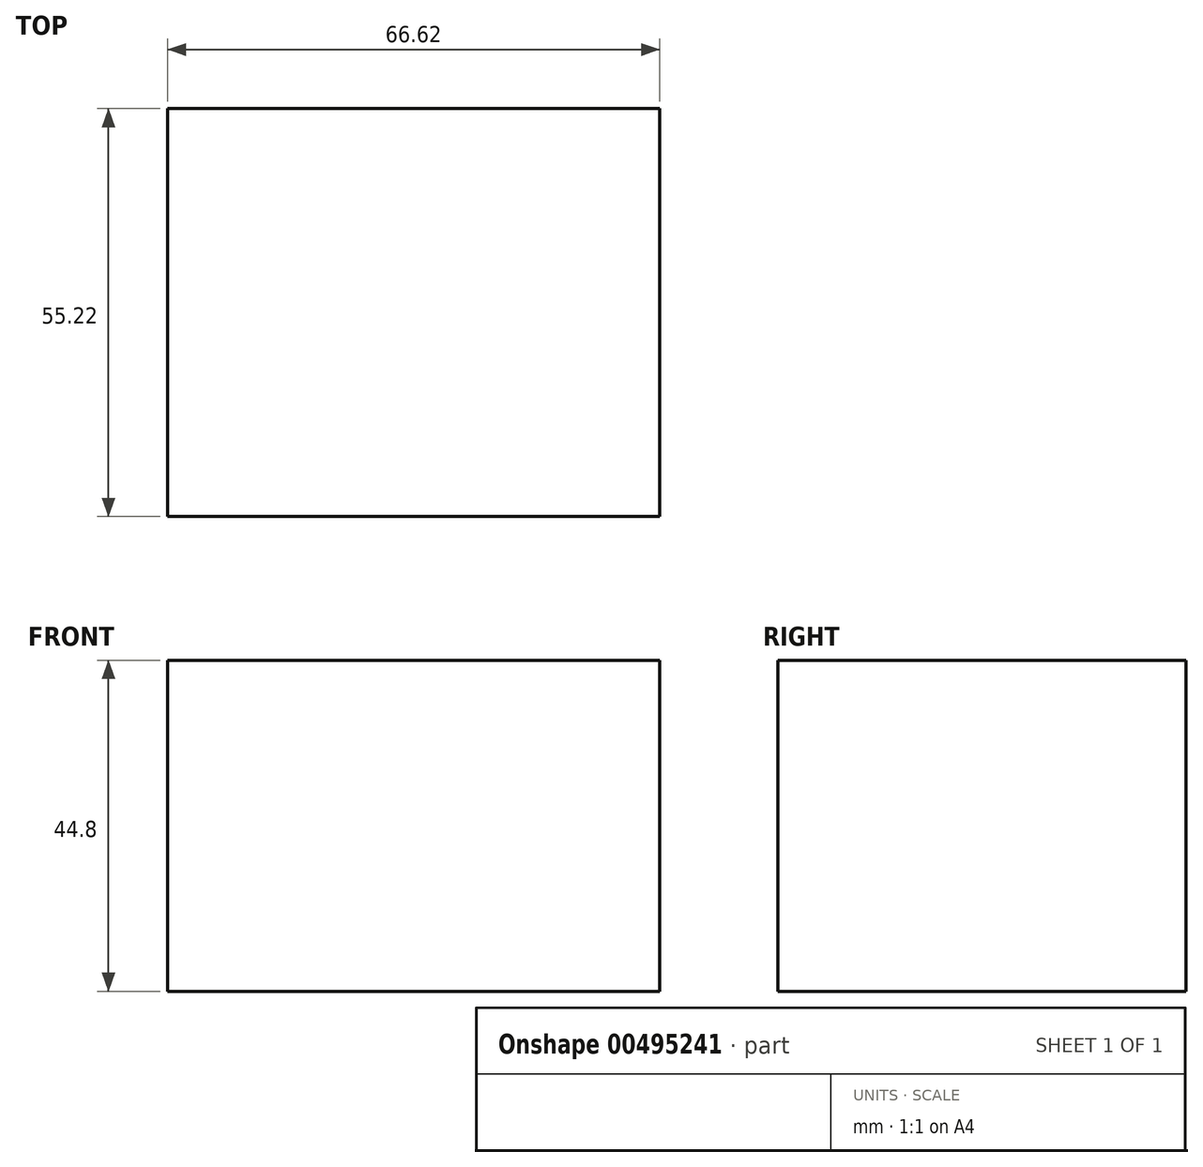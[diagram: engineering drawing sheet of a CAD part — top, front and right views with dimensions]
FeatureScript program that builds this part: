
annotation { "Feature Type Name" : "Feature", "Feature Type Description" : "" }
export const myFeature = defineFeature(function(context is Context, id is Id, definition is map)
    precondition{}
    {
        {
            var Q0;
            Q0=qCreatedBy(makeId("Top.planeOp"),FACE);
            var sketch = newSketch(context, id + "F0", { "sketchPlane" : qUnion([Q0])});
            skLineSegment(sketch, "E0.bottom", {"start": v(33.31, -27.61) * mm, "end": v(-33.31, -27.61) * mm});
            skLineSegment(sketch, "E0.top", {"start": v(33.31, 27.61) * mm, "end": v(-33.31, 27.61) * mm});
            skLineSegment(sketch, "E0.left", {"start": v(33.31, -27.61) * mm, "end": v(33.31, 27.61) * mm});
            skLineSegment(sketch, "E0.right", {"start": v(-33.31, -27.61) * mm, "end": v(-33.31, 27.61) * mm});
            skPoint(sketch, "E0.middle", {"position": v(0, 0) * mm});
            skSolve(sketch);
        }
        {
            var Q0;
            Q0=makeQuery(id+"F0.imprint","IMPRINT",FACE,{"disambiguationData":[TD([[makeQuery(id+"F0.imprint","IMPRINT",EDGE,{"derivedFrom":sQuery(id+"F0.wireOp",EDGE,"E0.bottom")}),-1.0]])]});
            extrude(context, id + "F1", {"entities" : qUnion([Q0]), "depth" : 44.8 * mm, "offsetDistance" : 25 * mm});
        }
    });
